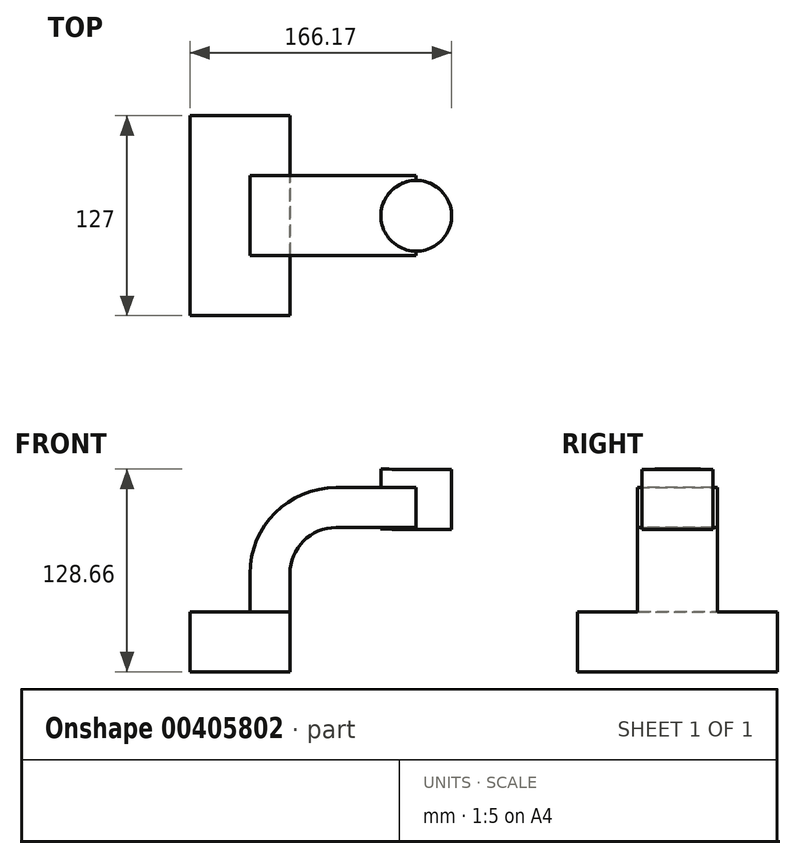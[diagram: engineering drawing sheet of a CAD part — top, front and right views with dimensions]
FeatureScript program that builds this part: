
annotation { "Feature Type Name" : "Feature", "Feature Type Description" : "" }
export const myFeature = defineFeature(function(context is Context, id is Id, definition is map)
    precondition{}
    {
        {
            var Q0;
            Q0=qCreatedBy(makeId("Front.planeOp"),FACE);
            var sketch = newSketch(context, id + "F0", { "sketchPlane" : qUnion([Q0])});
            skLineSegment(sketch, "E0.bottom", {"start": v(31.75, -19.05) * mm, "end": v(-31.75, -19.05) * mm});
            skLineSegment(sketch, "E0.top", {"start": v(31.75, 19.05) * mm, "end": v(-31.75, 19.05) * mm});
            skLineSegment(sketch, "E0.left", {"start": v(31.75, -19.05) * mm, "end": v(31.75, 19.05) * mm});
            skLineSegment(sketch, "E0.right", {"start": v(-31.75, -19.05) * mm, "end": v(-31.75, 19.05) * mm});
            skPoint(sketch, "E0.middle", {"position": v(0, 0) * mm});
            skLineSegment(sketch, "E1.bottom", {"start": v(134.42, 71.44) * mm, "end": v(78.54, 71.44) * mm});
            skLineSegment(sketch, "E1.top", {"start": v(134.42, 109.54) * mm, "end": v(78.54, 109.54) * mm});
            skLineSegment(sketch, "E1.left", {"start": v(134.42, 71.44) * mm, "end": v(134.42, 109.54) * mm});
            skLineSegment(sketch, "E1.right", {"start": v(78.54, 71.44) * mm, "end": v(78.54, 109.54) * mm});
            skPoint(sketch, "E1.middle", {"position": v(106.48, 90.49) * mm});
            skLineSegment(sketch, "E2", {"start": v(31.75, 19.05) * mm, "end": v(31.75, 43.2) * mm});
            skArc(sketch, "E3", {"start": v(31.75, 43.2) * mm, "mid": v(40.35, 63.97) * mm, "end": v(61.13, 72.57) * mm});
            skLineSegment(sketch, "E4", {"start": v(61.13, 72.57) * mm, "end": v(111.96, 72.57) * mm});
            skLineSegment(sketch, "E5.0", {"start": v(61.13, 97.97) * mm, "end": v(111.96, 97.97) * mm});
            skArc(sketch, "E5.1", {"start": v(6.35, 43.2) * mm, "mid": v(22.4, 81.93) * mm, "end": v(61.13, 97.97) * mm});
            skLineSegment(sketch, "E5.2", {"start": v(6.35, 19.05) * mm, "end": v(6.35, 43.2) * mm});
            skLineSegment(sketch, "E6", {"start": v(111.9, 71.44) * mm, "end": v(111.96, 109.54) * mm});
            skFitSpline(sketch, "E7", {"points": [v(-31.75, 19.05) * mm, v(78.54, 97.97) * mm], "startDerivative": vector(-6.4, 131.43) * mm, "endDerivative": vector(164.73, -56.5) * mm});
            skSolve(sketch);
        }
        {
            var Q0;
            Q0=makeQuery(id+"F0.imprint","IMPRINT",FACE,{"disambiguationData":[TD([[makeQuery(id+"F0.imprint","IMPRINT",EDGE,{"derivedFrom":sQuery(id+"F0.wireOp",EDGE,"E0.bottom")}),-1.0]])]});
            extrude(context, id + "F1", {"entities" : qUnion([Q0]), "endBound" : BoundingType.SYMMETRIC, "oppositeDirection" : true, "depth" : 127 * mm});
        }
        {
            var Q0;
            {var subQ1=sQuery(id+"F0.wireOp",EDGE,"E2");Q0=makeQuery(id+"F0.imprint","IMPRINT",FACE,{"disambiguationData":[TD([[makeQuery(id+"F0.imprint","IMPRINT",EDGE,{"derivedFrom":subQ1}),1.0]])]});}
            var Q1;
            {var subQ1=sQuery(id+"F0.wireOp",EDGE,"E1.right");var subQ3=sQuery(id+"F0.wireOp",EDGE,"E4");var subQ4=makeQuery(id+"F0.imprint","INTERSECT",VERTEX,{"derivedFrom":[subQ1,subQ3]});Q1=makeQuery(id+"F0.imprint","IMPRINT",FACE,{"disambiguationData":[TD([[makeQuery(id+"F0.imprint","IMPRINT",EDGE,{"disambiguationData":[TD([[subQ4,-1.0]])],"derivedFrom":subQ3}),1.0]])]});}
            extrude(context, id + "F2", {"entities" : qUnion([Q0, Q1]), "operationType" : NewBodyOperationType.ADD, "endBound" : BoundingType.SYMMETRIC, "depth" : 50.8 * mm});
        }
        {
            var Q0;
            {var subQ1=sQuery(id+"F0.wireOp",EDGE,"E5.1");Q0=makeQuery(id+"F0.imprint","IMPRINT",FACE,{"disambiguationData":[TD([[makeQuery(id+"F0.imprint","IMPRINT",EDGE,{"derivedFrom":subQ1}),1.0]])]});}
            extrude(context, id + "F3", {"entities" : qUnion([Q0]), "operationType" : NewBodyOperationType.ADD, "endBound" : BoundingType.SYMMETRIC, "depth" : 12.7 * mm});
        }
        {
            var Q0;
            {var subQ4=sQuery(id+"F0.wireOp",EDGE,"E1.left");Q0=makeQuery(id+"F0.imprint","IMPRINT",FACE,{"disambiguationData":[TD([[makeQuery(id+"F0.imprint","IMPRINT",EDGE,{"derivedFrom":subQ4}),1.0]])]});}
            var Q1;
            Q1=sQuery(id+"F0.wireOp",EDGE,"E6");
            revolve(context, id + "F4", {"operationType" : NewBodyOperationType.ADD, "entities" : qUnion([Q0]), "axis" : qUnion([Q1]), "revolveType" : RevolveType.FULL});
        }
    });
